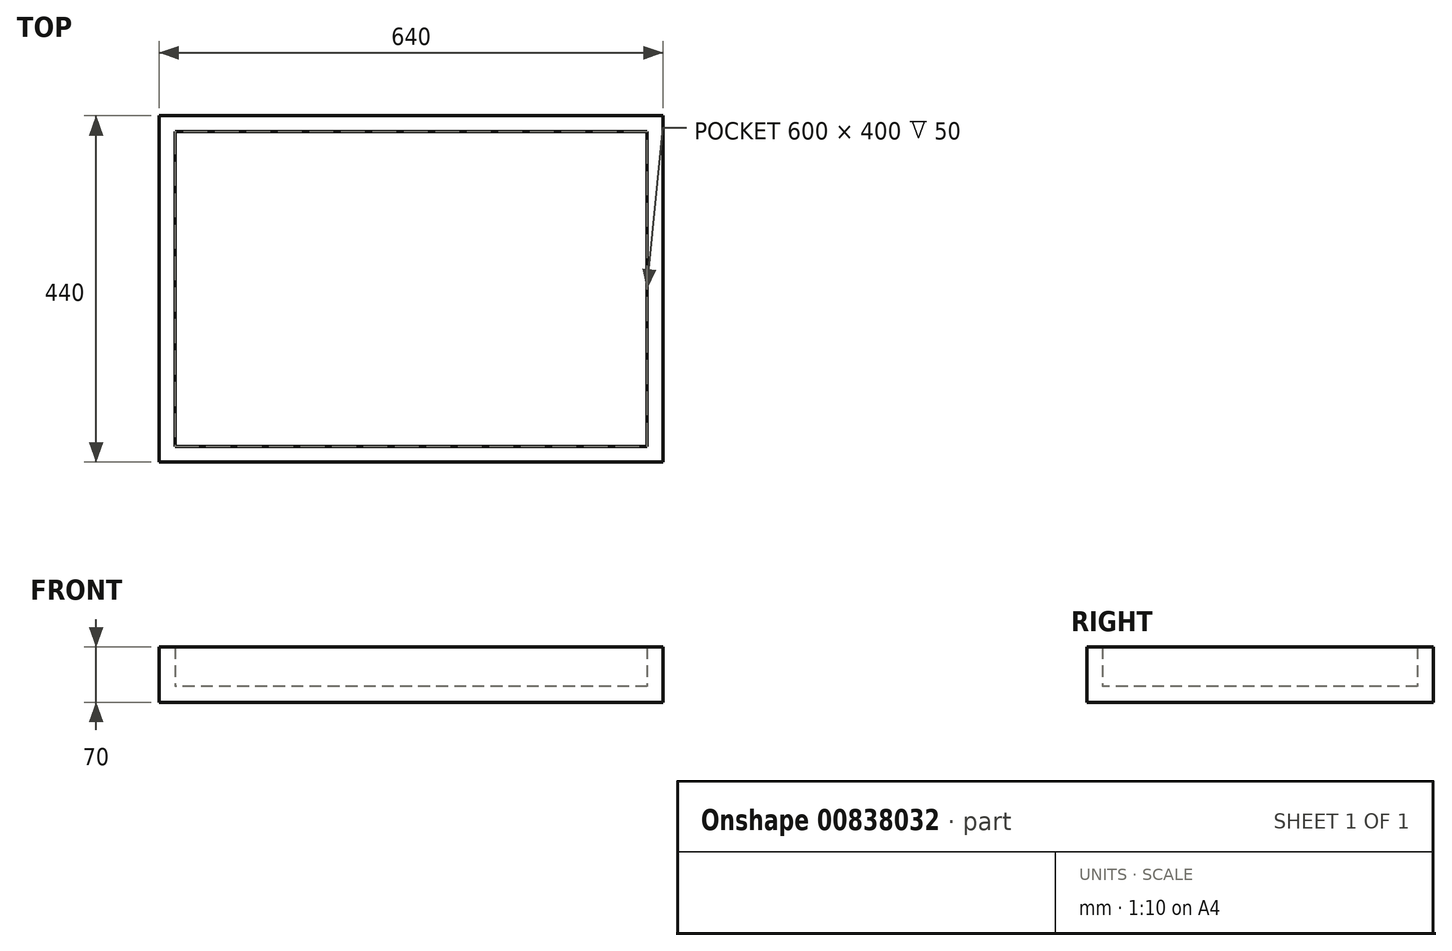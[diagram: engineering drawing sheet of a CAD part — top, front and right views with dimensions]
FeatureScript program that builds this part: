
annotation { "Feature Type Name" : "Feature", "Feature Type Description" : "" }
export const myFeature = defineFeature(function(context is Context, id is Id, definition is map)
    precondition{}
    {
        {
            var Q0;
            Q0=qCreatedBy(makeId("Top.planeOp"),FACE);
            var sketch = newSketch(context, id + "F0", { "sketchPlane" : qUnion([Q0])});
            skLineSegment(sketch, "E0.bottom", {"start": v(320, 220) * mm, "end": v(-320, 220) * mm});
            skLineSegment(sketch, "E0.top", {"start": v(320, -220) * mm, "end": v(-320, -220) * mm});
            skLineSegment(sketch, "E0.left", {"start": v(320, 220) * mm, "end": v(320, -220) * mm});
            skLineSegment(sketch, "E0.right", {"start": v(-320, 220) * mm, "end": v(-320, -220) * mm});
            skPoint(sketch, "E0.middle", {"position": v(0, 0) * mm});
            skSolve(sketch);
        }
        {
            var Q0;
            Q0=makeQuery(id+"F0.imprint","IMPRINT",FACE,{"disambiguationData":[TD([[makeQuery(id+"F0.imprint","IMPRINT",EDGE,{"derivedFrom":sQuery(id+"F0.wireOp",EDGE,"E0.bottom")}),1.0]])]});
            var Q1;
            Q1 = qSketchRegion(id + "F0", true);
            extrude(context, id + "F1", {"entities" : qUnion([Q0, Q1]), "depth" : 70 * mm, "offsetDistance" : 25 * mm});
        }
        {
            var Q0;
            Q0=makeQuery(id+"F1.opExtrude","CAP_FACE",FACE,{"disambiguationData":[OSD([sQuery(id+"F0.wireOp",EDGE,"E0.bottom"),sQuery(id+"F0.wireOp",EDGE,"E0.top"),sQuery(id+"F0.wireOp",EDGE,"E0.left"),sQuery(id+"F0.wireOp",EDGE,"E0.right")])],"isStart":false});
            shell(context, id + "F2", {"entities" : qUnion([Q0]), "thickness" : 20 * mm});
        }
    });
